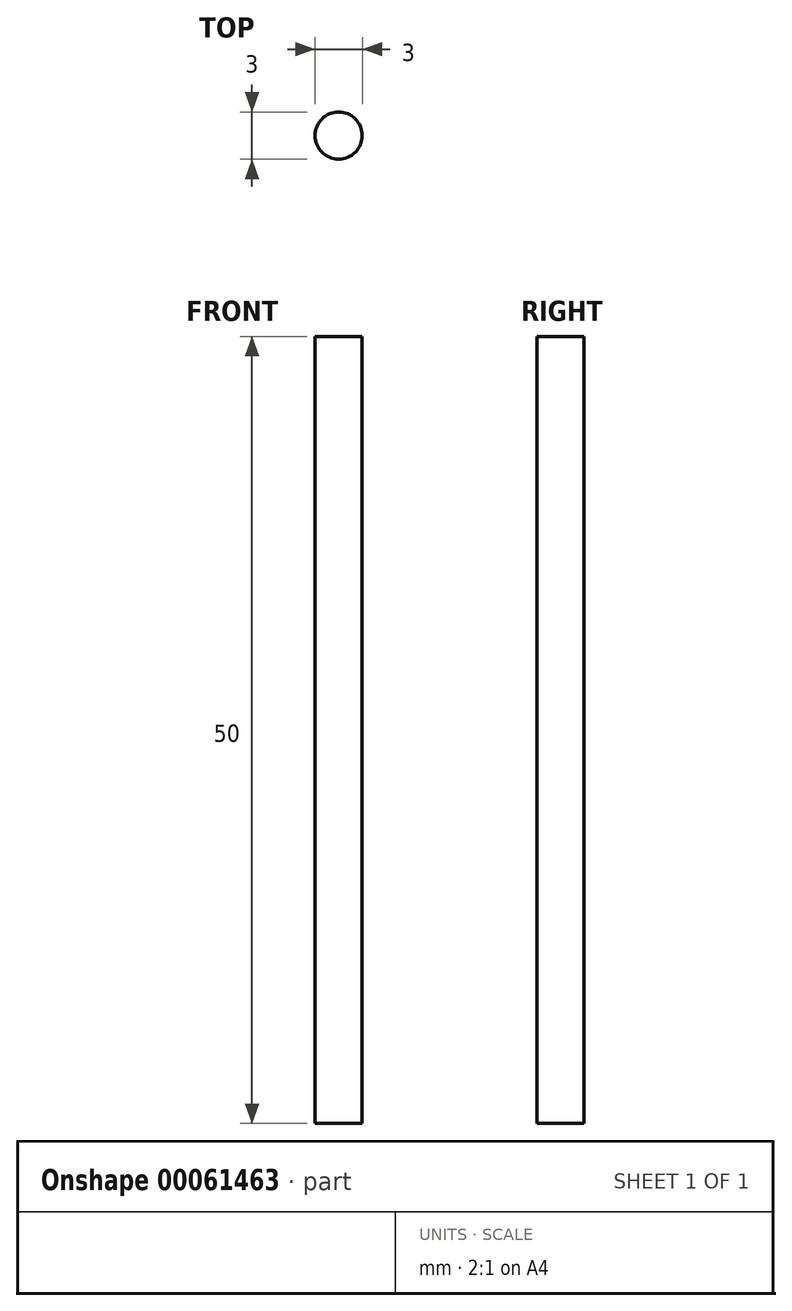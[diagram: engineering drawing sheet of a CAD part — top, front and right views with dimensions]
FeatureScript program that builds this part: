
annotation { "Feature Type Name" : "Feature", "Feature Type Description" : "" }
export const myFeature = defineFeature(function(context is Context, id is Id, definition is map)
    precondition{}
    {
        {
            var Q0;
            Q0=qCreatedBy(makeId("Top.planeOp"),FACE);
            var sketch = newSketch(context, id + "F0", { "sketchPlane" : qUnion([Q0])});
            skCircle(sketch, "E0", {"center": v(-0.88, 0.7) * mm, "radius": 1.5 * mm});
            skArc(sketch, "E1", {"start": v(-4.44, -5.4) * mm, "mid": v(0.66, -4.05) * mm, "end": v(5.58, -2.15) * mm});
            skLineSegment(sketch, "E2", {"start": v(5.58, -2.15) * mm, "end": v(3.52, 2.4) * mm});
            skLineSegment(sketch, "E3", {"start": v(3.52, 2.4) * mm, "end": v(3.5, 2.4) * mm});
            skArc(sketch, "E4", {"start": v(3.5, 2.4) * mm, "mid": v(0.68, 5.13) * mm, "end": v(-3.23, 4.77) * mm});
            skArc(sketch, "E5", {"start": v(-3.23, 4.77) * mm, "mid": v(-5.22, 2.5) * mm, "end": v(-5.43, -0.5) * mm});
            skLineSegment(sketch, "E6", {"start": v(-5.43, -0.5) * mm, "end": v(-5.45, -0.5) * mm});
            skLineSegment(sketch, "E7", {"start": v(-5.45, -0.5) * mm, "end": v(-4.44, -5.4) * mm});
            skSolve(sketch);
        }
        {
            var Q0;
            Q0=makeQuery(id+"F0.imprint","IMPRINT",FACE,{"disambiguationData":[TD([[makeQuery(id+"F0.imprint","IMPRINT",EDGE,{"derivedFrom":sQuery(id+"F0.wireOp",EDGE,"E0")}),1.0]])]});
            extrude(context, id + "F1", {"entities" : qUnion([Q0]), "depth" : 50 * mm});
        }
    });
